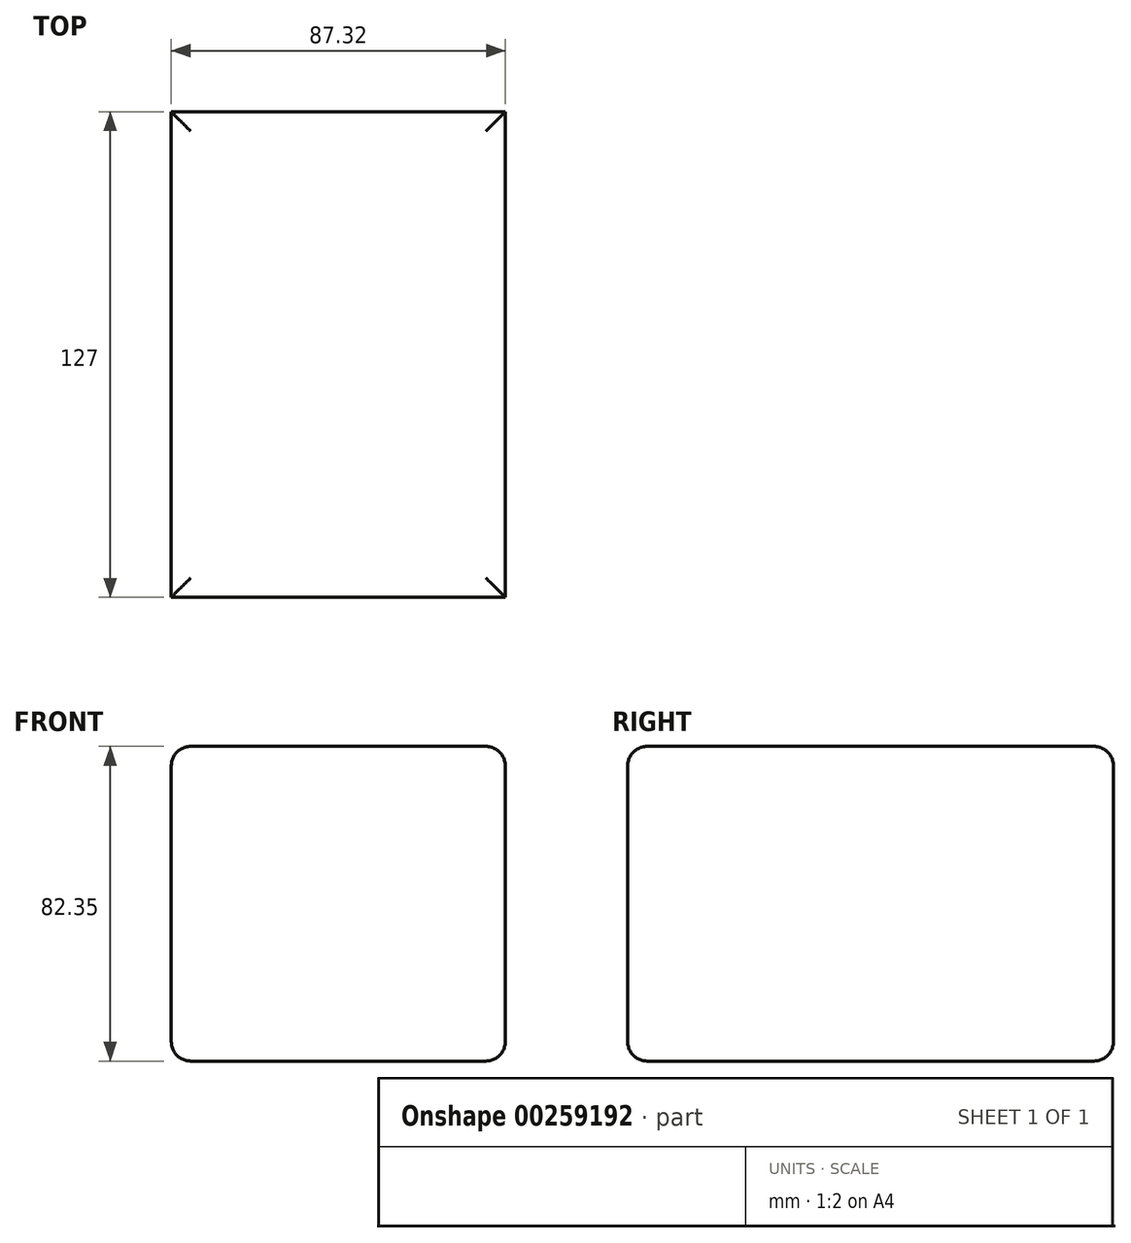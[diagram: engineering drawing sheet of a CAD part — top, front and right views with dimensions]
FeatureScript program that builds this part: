
annotation { "Feature Type Name" : "Feature", "Feature Type Description" : "" }
export const myFeature = defineFeature(function(context is Context, id is Id, definition is map)
    precondition{}
    {
        {
            var Q0;
            Q0=qCreatedBy(makeId("Front.planeOp"),FACE);
            var sketch = newSketch(context, id + "F0", { "sketchPlane" : qUnion([Q0])});
            skLineSegment(sketch, "E0.bottom", {"start": v(-40.82, 43.76) * mm, "end": v(46.5, 43.76) * mm});
            skLineSegment(sketch, "E0.top", {"start": v(-40.82, -38.6) * mm, "end": v(46.5, -38.6) * mm});
            skLineSegment(sketch, "E0.left", {"start": v(-40.82, 43.76) * mm, "end": v(-40.82, -38.6) * mm});
            skLineSegment(sketch, "E0.right", {"start": v(46.5, 43.76) * mm, "end": v(46.5, -38.6) * mm});
            skSolve(sketch);
        }
        {
            var Q0;
            Q0=makeQuery(id+"F0.imprint","IMPRINT",FACE,{"disambiguationData":[TD([[makeQuery(id+"F0.imprint","IMPRINT",EDGE,{"derivedFrom":sQuery(id+"F0.wireOp",EDGE,"E0.bottom")}),-1.0]])]});
            extrude(context, id + "F1", {"entities" : qUnion([Q0]), "depth" : 127 * mm});
        }
        {
            var Q0;
            Q0=makeQuery(id+"F1.opExtrude","SWEPT_EDGE",EDGE,{"disambiguationData":[OSD([sQuery(id+"F0.wireOp",EDGE,"E0.bottom"),sQuery(id+"F0.wireOp",EDGE,"E0.right")])]});
            var Q1;
            Q1=makeQuery(id+"F1.opExtrude","SWEPT_FACE",FACE,{"disambiguationData":[OSD([sQuery(id+"F0.wireOp",EDGE,"E0.top")])]});
            var Q2;
            Q2=makeQuery(id+"F1.opExtrude","CAP_EDGE",EDGE,{"disambiguationData":[OSD([sQuery(id+"F0.wireOp",EDGE,"E0.top")])],"isStart":true});
            var Q3;
            Q3=makeQuery(id+"F1.opExtrude","CAP_EDGE",EDGE,{"disambiguationData":[OSD([sQuery(id+"F0.wireOp",EDGE,"E0.bottom")])],"isStart":true});
            var Q4;
            Q4=makeQuery(id+"F1.opExtrude","SWEPT_EDGE",EDGE,{"disambiguationData":[OSD([sQuery(id+"F0.wireOp",EDGE,"E0.bottom"),sQuery(id+"F0.wireOp",EDGE,"E0.left")])]});
            var Q5;
            Q5=makeQuery(id+"F1.opExtrude","CAP_EDGE",EDGE,{"disambiguationData":[OSD([sQuery(id+"F0.wireOp",EDGE,"E0.bottom")])],"isStart":false});
            var Q6;
            Q6=makeQuery(id+"F1.opExtrude","SWEPT_EDGE",EDGE,{"disambiguationData":[OSD([sQuery(id+"F0.wireOp",EDGE,"E0.top"),sQuery(id+"F0.wireOp",EDGE,"E0.left")])]});
            fillet(context, id + "F2", {"entities" : qUnion([Q0, Q1, Q2, Q3, Q4, Q5, Q6]), "radius" : 5.08 * mm, "tangentPropagation" : true, "allowEdgeOverflow" : false});
        }
    });
